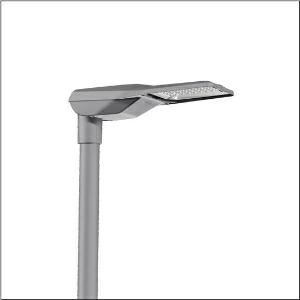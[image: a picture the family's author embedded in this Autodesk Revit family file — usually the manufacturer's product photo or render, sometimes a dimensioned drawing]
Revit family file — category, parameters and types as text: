
# Revit family: streetlight_sl_21_iq_mini___st1_0a_5xe2d61d08hb_7283
name_source: partatom
category: Lighting Fixtures
units: mm (PartAtom-declared; Revit-internal decimal feet)

## family parameters
Cut with Voids When Loaded = No
Host = Face
Light Source = No
Part Type = Normal
Room Calculation Point = No
Round Connector Dimension = Use Diameter
Shared = No

## types (1)
- --- (1 x LED, 8480 lm, 70.9 W, 2700K)
    Apparent Load = 71 VA
    CIE Flux Codes = 37 72 97 100 100
    Color Rendering = 70
    Color Temperature = 2700K
    Default Elevation = 1800 mm
    Description = Streetlight SL 21 iQ mini, mast luminaire, primary light control with lens, of PMMA, primary optical cover: cover, of toughened safety glass, transparent, light distribution: ST1.0a, light emission: direct distribution, primary light characteristic: asymmetric, installation type: post-top, side-entry, LED, High Power LED, rated luminous flux: 8.480lm, luminous efficacy: 120lm/W, light colour: 727, colour temperature: 2700K, control: Auto-Match, Temp-Guard, Lumen-Switch, Night-Set, Smart-Wire, Light-Fading, Desk-Remote (wireless, voltage-free reading and setting of iQ features in the workshop via application-optimized NFC function/RFID function), optimised constant luminous flux control (CLO 2.0), presetting dimming linear, mains connection: 220..240V, AC, 50/60Hz, start of lifetime: 71W, end of service life: 75W, reduction: 31W, luminaire housing, of diecast aluminium, powder-coated, Siteco® metallic grey (DB 702S), corrosivity category C5 mid according to DIN EN ISO 12944, please order mast flange separately, inclination adjustable: 0°, 5°, 10°, 15°, sealing non-destructively replaceable, multi-level sealing system, length: 628mm, width: 235mm, height: 110mm, mast flange for spigot size: 42mm (side-entry): 5XC10008XM4, 60/48mm (side-entry/post-top): 5XC10108XM2, 76/60mm (side-entry/post-top): 5XC10108XM1, protection rating (complete): IP66, insulation class (complete): insulation class II (safety insulation), certification: CE, ENEC, ENEC+, VDE, impact resistance: IK09, permissible operating ambient temperature for outdoor applications: -40..+50°C, standard-compliant lighting for roads and squares, packaging unit: 1 piece

Light Distribution: ST1.0a
    Height = 110 mm
    Lamp = 1 x LED
    Lamp Light Flux = 8480 lm
    Lamp Power = 70.9 W
    Lamp count = 1
    Length = 625 mm
    Luminous efficacy = 120 lm/W
    Manufacturer = Siteco
    ModVariant = No
    Model = 5XE2D61D08HB
    Number of Poles = 1
    OnlyDefault = Yes
    Power Factor = 1
    Product Name = Streetlight SL 21 iQ mini | ST1.0a
    Product group = mast luminaire | pylon top
    ProductGroupID = 6100
    Protection Class = Protection class II
    Protection Degree = IP 66
    RLX_Detail_Level = 1
    RLX_Emergency_Light_Flux = 0 lm
    RLX_Emergency_Type = 0
    RLX_Emergency_Type_DB = No
    RlxData = <blob elided: 92089 chars, md5=41faffa1>
    Socket = socket
    Standby Power = 0 W
    System Light Flux = 8480 lm
    System Power = 71 W
    Type Comments = factory setting: luminous flux: 100 % | dim-lin: 254 | 711 mA
    Type Image = l_1003519.jpg
    URL = http://relux.com
    VarID = @adj_108423
    Voltage = 0 V
    Weight = 0.00 kg
    Width = 234 mm

## geometry (parser evidence)
native form markers: Blend x4, Sweep x11
no freeform markers — native parametric forms only
